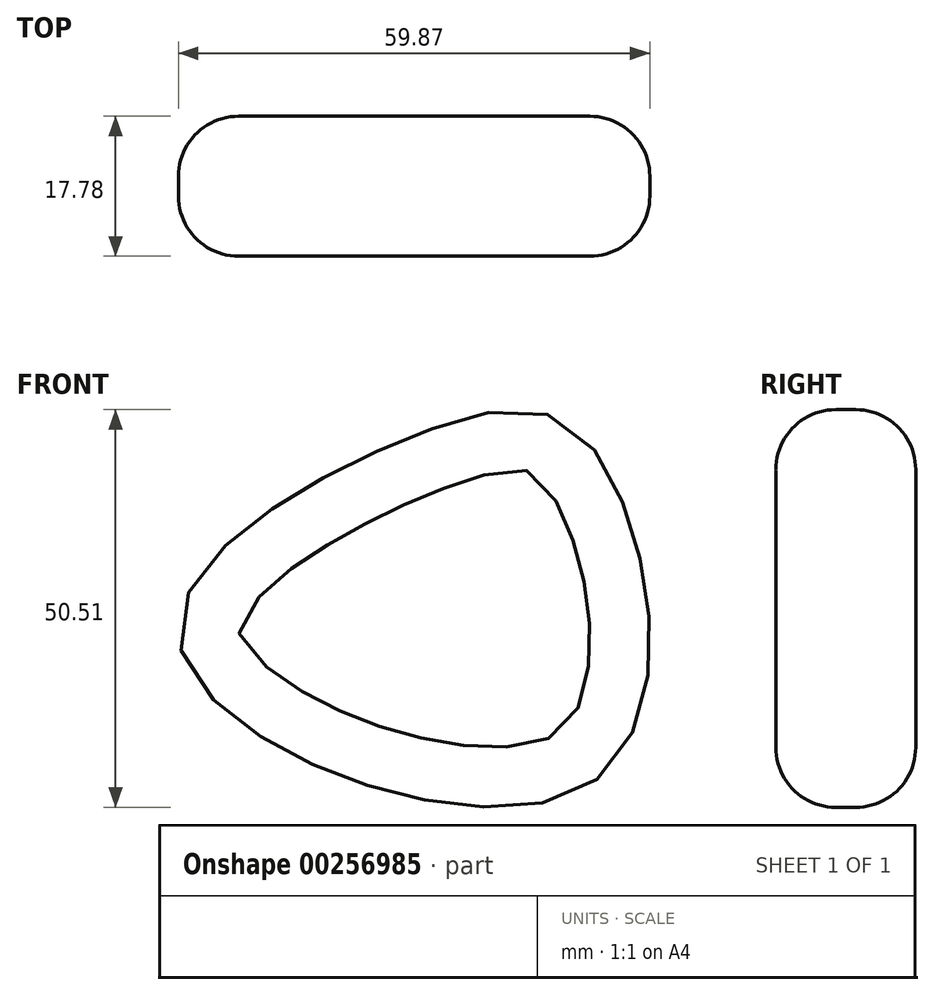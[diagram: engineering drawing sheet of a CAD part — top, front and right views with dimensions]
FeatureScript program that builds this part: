
annotation { "Feature Type Name" : "Feature", "Feature Type Description" : "" }
export const myFeature = defineFeature(function(context is Context, id is Id, definition is map)
    precondition{}
    {
        {
            var Q0;
            Q0=qCreatedBy(makeId("Front.planeOp"),FACE);
            var sketch = newSketch(context, id + "F0", { "sketchPlane" : qUnion([Q0])});
            skFitSpline(sketch, "E0", {"points": [v(0, 0) * mm, v(30.54, 27.66) * mm, v(52.67, 25.19) * mm, v(51.9, -17.04) * mm, v(0, 0) * mm]});
            skSolve(sketch);
        }
        {
            var Q0;
            Q0=makeQuery(id+"F0.imprint","IMPRINT",FACE,{"disambiguationData":[TD([[makeQuery(id+"F0.imprint","IMPRINT",EDGE,{"derivedFrom":sQuery(id+"F0.wireOp",EDGE,"E0")}),-1.0]])]});
            extrude(context, id + "F1", {"entities" : qUnion([Q0]), "depth" : 17.78 * mm});
        }
        {
            var Q0;
            Q0=makeQuery(id+"F1.opExtrude","CAP_FACE",FACE,{"disambiguationData":[OSD([sQuery(id+"F0.wireOp",EDGE,"E0")])],"isStart":false});
            var Q1;
            Q1=makeQuery(id+"F1.opExtrude","CAP_EDGE",EDGE,{"disambiguationData":[OSD([sQuery(id+"F0.wireOp",EDGE,"E0")])],"isStart":true});
            fillet(context, id + "F2", {"entities" : qUnion([Q0, Q1]), "radius" : 7.62 * mm, "tangentPropagation" : true, "allowEdgeOverflow" : false});
        }
    });
